# Revit family: Door_Overhead-Swing_Renlita_S-1000_Glazed
name_source: partatom
category: Doors
units: mm (PartAtom-declared; Revit-internal decimal feet)

## family parameters
Always vertical = Yes
Classification Number = 23.30.10.17.37
Cut with Voids When Loaded = No
Host = Wall
Room Calculation Point = No
Shared = No

## types (2) — shared parameters
Assembly Code = B2030
Clear Opening Width = 7' - 7"
Clearance Material = ARCAT Clearance
Description = Renlita Overhead Swing Single Panel Door - S-1000 as Specified
Door Panel Design = s1000PanelGlazed : Frame with Windows
Exterior Finish = Metal - Renlita - White
Face Thickness_Exterior = 0' - 2"
Fire Rating = as Specified
Frame Finish = Metal - Renlita - White
Function = Interior
Glazing Tint = Glass - Clear
Height = 8' - 0"
Interior Finish = Metal - Renlita - White
Keynote = 8000
Manufacturer = Renlita Doors North America, LLC
Manufacturer Fax = 903-583-7544
Manufacturer Website = http://www.renlitadoors.com
Max Height = 20' - 0"
Max Width = 30' - 0"
Maximum Size = 30' W x 20' H
Model = as Specified
Offset from Wall Notes = Use Positive or Negative values to determine location
Opening Height = 8' - 0"
Opening Width = 8' - 0"
Panel Height = 7' - 11 1/2"
Panel Width = 7' - 11"
Product Data = http://www.arcat.com
Projection_Exterior = 3' - 9 9/16"
Projection_Interior = -4' - 2 7/16"
Rough Height = 0' - 0"
Rough Width = 0' - 0"
Sales Information = http://www.renlitadoors.com
Thickness = 0' - 0"
URL = http://www.renlitadoors.com
Wall Closure = By host
Weatherstripping Color = Finish - Black
Width = 8' - 0"
panellocationwhenopen = 0' - 2 1/2"
zero-valued in all types: Expected Lifespan (Years), Maintenance Schedule (Months), R-Value, Warranty Duration (Years)

## per-type parameters (varying)
| type | Glazing Thickness | Motorized |
| Manual Operation | 0' - 0" | No |
| Motorized | 0' - 0 1/4" | Yes |

## geometry (parser evidence)
native form markers: Blend x14, Sweep x12
no freeform markers — native parametric forms only
